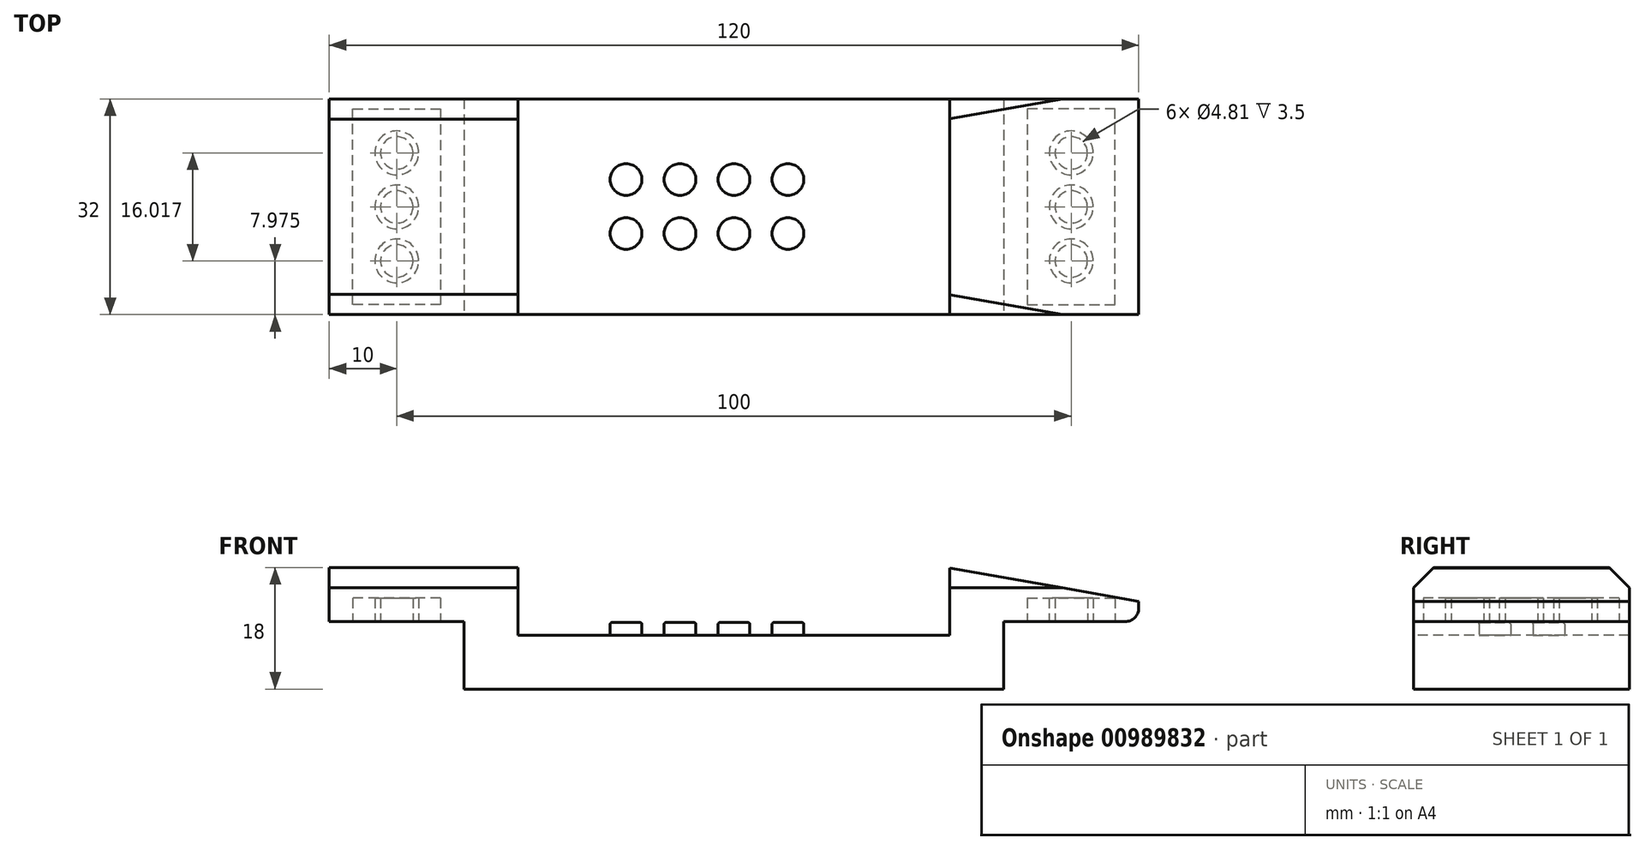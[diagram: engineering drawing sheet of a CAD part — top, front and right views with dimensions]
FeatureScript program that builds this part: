
annotation { "Feature Type Name" : "Feature", "Feature Type Description" : "" }
export const myFeature = defineFeature(function(context is Context, id is Id, definition is map)
    precondition{}
    {
        {
            var Q0;
            Q0=qCreatedBy(makeId("Front.planeOp"),FACE);
            var sketch = newSketch(context, id + "F0", { "sketchPlane" : qUnion([Q0])});
            skLineSegment(sketch, "E0", {"start": v(0, 0) * mm, "end": v(-40, 0) * mm});
            skLineSegment(sketch, "E1", {"start": v(-40, 0) * mm, "end": v(-40, 10) * mm});
            skLineSegment(sketch, "E2", {"start": v(-40, 10) * mm, "end": v(-60, 10) * mm});
            skLineSegment(sketch, "E3.0", {"start": v(-32, 18) * mm, "end": v(-60, 18) * mm});
            skLineSegment(sketch, "E3.1", {"start": v(-32, 8) * mm, "end": v(-32, 18) * mm});
            skLineSegment(sketch, "E3.2", {"start": v(0, 8) * mm, "end": v(-32, 8) * mm});
            skLineSegment(sketch, "E4", {"start": v(-60, 18) * mm, "end": v(-60, 10) * mm});
            skLineSegment(sketch, "E5", {"start": v(0, 8) * mm, "end": v(0, 0) * mm});
            skCircle(sketch, "E6", {"center": v(-50, 6) * mm, "radius": 10 * mm, "construction": true});
            skPoint(sketch, "E6.centerSnap0", {"position": v(-50, 10) * mm});
            skCircle(sketch, "E7", {"center": v(-50, 6) * mm, "radius": 12 * mm, "construction": true});
            skSolve(sketch);
        }
        {
            var Q0;
            Q0=makeQuery(id+"F0.imprint","IMPRINT",FACE,{"disambiguationData":[TD([[makeQuery(id+"F0.imprint","IMPRINT",EDGE,{"derivedFrom":sQuery(id+"F0.wireOp",EDGE,"E0")}),-1.0]])]});
            extrude(context, id + "F1", {"entities" : qUnion([Q0]), "oppositeDirection" : true, "depth" : 32 * mm, "offsetDistance" : 25 * mm});
        }
        {
            var Q0;
            Q0=makeQuery(id+"F1.opExtrude","SWEPT_FACE",FACE,{"disambiguationData":[OSD([sQuery(id+"F0.wireOp",EDGE,"E2")])]});
            var sketch = newSketch(context, id + "F2", { "sketchPlane" : qUnion([Q0])});
            skLineSegment(sketch, "E8", {"start": v(-43.5, -1.47) * mm, "end": v(-56.5, -1.47) * mm});
            skLineSegment(sketch, "E9", {"start": v(-56.5, -1.47) * mm, "end": v(-56.5, -30.5) * mm});
            skLineSegment(sketch, "E10", {"start": v(-56.5, -30.5) * mm, "end": v(-43.5, -30.5) * mm});
            skLineSegment(sketch, "E11", {"start": v(-43.5, -30.5) * mm, "end": v(-43.5, -1.47) * mm});
            skCircle(sketch, "E12.0", {"center": v(-50, -7.97) * mm, "radius": 2.4 * mm});
            skCircle(sketch, "E13.0", {"center": v(-50, -7.97) * mm, "radius": 3.25 * mm});
            skCircle(sketch, "E14.0", {"center": v(-50, -15.98) * mm, "radius": 2.4 * mm});
            skCircle(sketch, "E15.0", {"center": v(-50, -15.98) * mm, "radius": 3.25 * mm});
            skCircle(sketch, "E16.0", {"center": v(-50, -24) * mm, "radius": 2.4 * mm});
            skCircle(sketch, "E17.0", {"center": v(-50, -24) * mm, "radius": 3.25 * mm});
            skLineSegment(sketch, "E18.0", {"start": v(-42, 0.03) * mm, "end": v(-42, -32) * mm, "construction": true});
            skLineSegment(sketch, "E18.1", {"start": v(-42, 0.03) * mm, "end": v(-58, 0.03) * mm, "construction": true});
            skLineSegment(sketch, "E18.2", {"start": v(-58, 0.03) * mm, "end": v(-58, -32) * mm, "construction": true});
            skLineSegment(sketch, "E18.3", {"start": v(-42, -32) * mm, "end": v(-58, -32) * mm, "construction": true});
            skSolve(sketch);
        }
        {
            var Q0;
            Q0=makeQuery(id+"F2.imprint","IMPRINT",FACE,{"disambiguationData":[TD([[makeQuery(id+"F2.imprint","IMPRINT",EDGE,{"derivedFrom":sQuery(id+"F2.wireOp",EDGE,"E8")}),1.0]])]});
            var Q1;
            Q1=makeQuery(id+"F2.imprint","IMPRINT",FACE,{"disambiguationData":[TD([[makeQuery(id+"F2.imprint","IMPRINT",EDGE,{"derivedFrom":sQuery(id+"F2.wireOp",EDGE,"E14.0")}),1.0]])]});
            var Q2;
            Q2=makeQuery(id+"F2.imprint","IMPRINT",FACE,{"disambiguationData":[TD([[makeQuery(id+"F2.imprint","IMPRINT",EDGE,{"derivedFrom":sQuery(id+"F2.wireOp",EDGE,"E12.0")}),1.0]])]});
            var Q3;
            Q3=makeQuery(id+"F2.imprint","IMPRINT",FACE,{"disambiguationData":[TD([[makeQuery(id+"F2.imprint","IMPRINT",EDGE,{"derivedFrom":sQuery(id+"F2.wireOp",EDGE,"E16.0")}),1.0]])]});
            extrude(context, id + "F3", {"entities" : qUnion([Q0, Q1, Q2, Q3]), "operationType" : NewBodyOperationType.REMOVE, "oppositeDirection" : true, "depth" : 3.5 * mm, "offsetDistance" : 25 * mm});
        }
        {
            var Q0;
            Q0=makeQuery(id+"F1.opExtrude","SWEPT_BODY",BODY,{"disambiguationData":[OSD([sQuery(id+"F0.wireOp",EDGE,"E0"),sQuery(id+"F0.wireOp",EDGE,"E1"),sQuery(id+"F0.wireOp",EDGE,"E2"),sQuery(id+"F0.wireOp",EDGE,"E3.0"),sQuery(id+"F0.wireOp",EDGE,"E3.1"),sQuery(id+"F0.wireOp",EDGE,"E3.2"),sQuery(id+"F0.wireOp",EDGE,"E4"),sQuery(id+"F0.wireOp",EDGE,"E5")])]});
            var Q1;
            Q1=makeQuery(id+"F1.opExtrude","SWEPT_FACE",FACE,{"disambiguationData":[OSD([sQuery(id+"F0.wireOp",EDGE,"E5")])]});
            mirror(context, id + "F4", {"operationType" : NewBodyOperationType.ADD, "entities" : qUnion([Q0]), "mirrorPlane" : qUnion([Q1])});
        }
        {
            var Q0;
            {var subQ0=makeQuery(id+"F1.opExtrude","SWEPT_FACE",FACE,{"disambiguationData":[OSD([sQuery(id+"F0.wireOp",EDGE,"E3.2")])]});Q0=makeQuery(id+"F4.boolean.opBoolean","MERGE",FACE,{"derivedFrom":[subQ0,makeQuery(id+"F4.opPattern","COPY",FACE,{"derivedFrom":subQ0,"instanceName":"1"})]});}
            var sketch = newSketch(context, id + "F5", { "sketchPlane" : qUnion([Q0])});
            skLineSegment(sketch, "E19.0", {"start": v(-19.9, 7.93) * mm, "end": v(12.1, 7.93) * mm, "construction": true});
            skLineSegment(sketch, "E19.1", {"start": v(-19.9, 7.93) * mm, "end": v(-19.9, 23.93) * mm, "construction": true});
            skLineSegment(sketch, "E19.2", {"start": v(-19.9, 23.93) * mm, "end": v(12.1, 23.93) * mm, "construction": true});
            skLineSegment(sketch, "E19.3", {"start": v(12.1, 7.93) * mm, "end": v(12.1, 23.93) * mm, "construction": true});
            skCircle(sketch, "E19.4", {"center": v(8, 12.03) * mm, "radius": 2.35 * mm});
            skCircle(sketch, "E19.5", {"center": v(8, 20.03) * mm, "radius": 2.35 * mm});
            skCircle(sketch, "E19.6", {"center": v(0, 20.03) * mm, "radius": 2.35 * mm});
            skCircle(sketch, "E19.7", {"center": v(0, 12.03) * mm, "radius": 2.35 * mm});
            skCircle(sketch, "E19.8", {"center": v(-8, 12.03) * mm, "radius": 2.35 * mm});
            skCircle(sketch, "E19.9", {"center": v(-8, 20.03) * mm, "radius": 2.35 * mm});
            skCircle(sketch, "E19.10", {"center": v(-16, 20.03) * mm, "radius": 2.35 * mm});
            skCircle(sketch, "E19.11", {"center": v(-16, 12.03) * mm, "radius": 2.35 * mm});
            skSolve(sketch);
        }
        {
            var Q0;
            Q0=makeQuery(id+"F5.imprint","IMPRINT",FACE,{"disambiguationData":[TD([[makeQuery(id+"F5.imprint","IMPRINT",EDGE,{"derivedFrom":sQuery(id+"F5.wireOp",EDGE,"E19.11")}),1.0]])]});
            var Q1;
            Q1=makeQuery(id+"F5.imprint","IMPRINT",FACE,{"disambiguationData":[TD([[makeQuery(id+"F5.imprint","IMPRINT",EDGE,{"derivedFrom":sQuery(id+"F5.wireOp",EDGE,"E19.10")}),1.0]])]});
            var Q2;
            Q2=makeQuery(id+"F5.imprint","IMPRINT",FACE,{"disambiguationData":[TD([[makeQuery(id+"F5.imprint","IMPRINT",EDGE,{"derivedFrom":sQuery(id+"F5.wireOp",EDGE,"E19.9")}),1.0]])]});
            var Q3;
            Q3=makeQuery(id+"F5.imprint","IMPRINT",FACE,{"disambiguationData":[TD([[makeQuery(id+"F5.imprint","IMPRINT",EDGE,{"derivedFrom":sQuery(id+"F5.wireOp",EDGE,"E19.8")}),1.0]])]});
            var Q4;
            Q4=makeQuery(id+"F5.imprint","IMPRINT",FACE,{"disambiguationData":[TD([[makeQuery(id+"F5.imprint","IMPRINT",EDGE,{"derivedFrom":sQuery(id+"F5.wireOp",EDGE,"E19.7")}),1.0]])]});
            var Q5;
            Q5=makeQuery(id+"F5.imprint","IMPRINT",FACE,{"disambiguationData":[TD([[makeQuery(id+"F5.imprint","IMPRINT",EDGE,{"derivedFrom":sQuery(id+"F5.wireOp",EDGE,"E19.6")}),1.0]])]});
            var Q6;
            Q6=makeQuery(id+"F5.imprint","IMPRINT",FACE,{"disambiguationData":[TD([[makeQuery(id+"F5.imprint","IMPRINT",EDGE,{"derivedFrom":sQuery(id+"F5.wireOp",EDGE,"E19.5")}),1.0]])]});
            var Q7;
            Q7=makeQuery(id+"F5.imprint","IMPRINT",FACE,{"disambiguationData":[TD([[makeQuery(id+"F5.imprint","IMPRINT",EDGE,{"derivedFrom":sQuery(id+"F5.wireOp",EDGE,"E19.4")}),1.0]])]});
            extrude(context, id + "F6", {"entities" : qUnion([Q0, Q1, Q2, Q3, Q4, Q5, Q6, Q7]), "operationType" : NewBodyOperationType.ADD, "depth" : 1.85 * mm, "offsetDistance" : 25 * mm});
        }
        {
            var Q0;
            Q0=makeQuery(id+"F1.opExtrude","CAP_EDGE",EDGE,{"disambiguationData":[OSD([sQuery(id+"F0.wireOp",EDGE,"E3.0")])],"isStart":true});
            var Q1;
            Q1=makeQuery(id+"F1.opExtrude","CAP_EDGE",EDGE,{"disambiguationData":[OSD([sQuery(id+"F0.wireOp",EDGE,"E3.0")])],"isStart":false});
            var Q2;
            Q2=makeQuery(id+"F4.opPattern","COPY",EDGE,{"derivedFrom":makeQuery(id+"F1.opExtrude","CAP_EDGE",EDGE,{"disambiguationData":[OSD([sQuery(id+"F0.wireOp",EDGE,"E3.0")])],"isStart":true}),"instanceName":"1"});
            var Q3;
            Q3=makeQuery(id+"F4.opPattern","COPY",EDGE,{"derivedFrom":makeQuery(id+"F1.opExtrude","CAP_EDGE",EDGE,{"disambiguationData":[OSD([sQuery(id+"F0.wireOp",EDGE,"E3.0")])],"isStart":false}),"instanceName":"1"});
            chamfer(context, id + "F7", {"entities" : qUnion([Q0, Q1, Q2, Q3]), "width" : 3 * mm, "tangentPropagation" : true});
        }
        {
            var Q0;
            {var subQ0=sQuery(id+"F0.wireOp",EDGE,"E4");Q0=makeQuery(id+"F7.opChamfer","BLEND_EDGE",EDGE,{"blendedFrom":[makeQuery(id+"F4.opPattern","COPY",EDGE,{"derivedFrom":makeQuery(id+"F1.opExtrude","SWEPT_EDGE",EDGE,{"disambiguationData":[OSD([sQuery(id+"F0.wireOp",EDGE,"E3.0"),subQ0])]}),"instanceName":"1"}),makeQuery(id+"F4.opPattern","COPY",FACE,{"derivedFrom":makeQuery(id+"F1.opExtrude","SWEPT_FACE",FACE,{"disambiguationData":[OSD([subQ0])]}),"instanceName":"1"})],"blendedInto":[makeQuery(id+"F4.opPattern","COPY",FACE,{"derivedFrom":makeQuery(id+"F1.opExtrude","SWEPT_FACE",FACE,{"disambiguationData":[OSD([subQ0])]}),"instanceName":"1"})]});}
            var Q1;
            Q1=makeQuery(id+"F4.opPattern","COPY",EDGE,{"derivedFrom":makeQuery(id+"F1.opExtrude","SWEPT_EDGE",EDGE,{"disambiguationData":[OSD([sQuery(id+"F0.wireOp",EDGE,"E2"),sQuery(id+"F0.wireOp",EDGE,"E4")])]}),"instanceName":"1"});
            var Q2;
            {var subQ0=sQuery(id+"F0.wireOp",EDGE,"E3.0");Q2=makeQuery(id+"F7.opChamfer","BLEND_EDGE",EDGE,{"blendedFrom":[makeQuery(id+"F4.opPattern","COPY",EDGE,{"derivedFrom":makeQuery(id+"F1.opExtrude","SWEPT_EDGE",EDGE,{"disambiguationData":[OSD([subQ0,sQuery(id+"F0.wireOp",EDGE,"E4")])]}),"instanceName":"1"}),makeQuery(id+"F4.opPattern","COPY",FACE,{"derivedFrom":makeQuery(id+"F1.opExtrude","SWEPT_FACE",FACE,{"disambiguationData":[OSD([subQ0])]}),"instanceName":"1"})],"blendedInto":[makeQuery(id+"F4.opPattern","COPY",FACE,{"derivedFrom":makeQuery(id+"F1.opExtrude","SWEPT_FACE",FACE,{"disambiguationData":[OSD([subQ0])]}),"instanceName":"1"})]});}
            fillet(context, id + "F8", {"entities" : qUnion([Q0, Q1, Q2]), "radius" : 2 * mm, "tangentPropagation" : true, "allowEdgeOverflow" : false});
        }
        {
            var Q0;
            Q0=makeQuery(id+"F4.opPattern","COPY",EDGE,{"derivedFrom":makeQuery(id+"F1.opExtrude","SWEPT_EDGE",EDGE,{"disambiguationData":[OSD([sQuery(id+"F0.wireOp",EDGE,"E3.0"),sQuery(id+"F0.wireOp",EDGE,"E4")])]}),"instanceName":"1"});
            chamfer(context, id + "F9", {"entities" : qUnion([Q0]), "chamferType" : ChamferType.OFFSET_ANGLE, "width" : 5 * mm, "oppositeDirection" : false, "angle" : 80 * degree, "tangentPropagation" : true});
        }
        {
            var Q0;
            Q0=makeQuery(id+"F6.opExtrude","CAP_EDGE",EDGE,{"disambiguationData":[OSD([sQuery(id+"F5.wireOp",EDGE,"E19.11")])],"isStart":false});
            var Q1;
            Q1=makeQuery(id+"F6.opExtrude","CAP_EDGE",EDGE,{"disambiguationData":[OSD([sQuery(id+"F5.wireOp",EDGE,"E19.10")])],"isStart":false});
            var Q2;
            Q2=makeQuery(id+"F6.opExtrude","CAP_EDGE",EDGE,{"disambiguationData":[OSD([sQuery(id+"F5.wireOp",EDGE,"E19.9")])],"isStart":false});
            var Q3;
            Q3=makeQuery(id+"F6.opExtrude","CAP_EDGE",EDGE,{"disambiguationData":[OSD([sQuery(id+"F5.wireOp",EDGE,"E19.8")])],"isStart":false});
            var Q4;
            Q4=makeQuery(id+"F6.opExtrude","CAP_EDGE",EDGE,{"disambiguationData":[OSD([sQuery(id+"F5.wireOp",EDGE,"E19.7")])],"isStart":false});
            var Q5;
            Q5=makeQuery(id+"F6.opExtrude","CAP_EDGE",EDGE,{"disambiguationData":[OSD([sQuery(id+"F5.wireOp",EDGE,"E19.4")])],"isStart":false});
            var Q6;
            Q6=makeQuery(id+"F6.opExtrude","CAP_EDGE",EDGE,{"disambiguationData":[OSD([sQuery(id+"F5.wireOp",EDGE,"E19.5")])],"isStart":false});
            var Q7;
            Q7=makeQuery(id+"F6.opExtrude","CAP_EDGE",EDGE,{"disambiguationData":[OSD([sQuery(id+"F5.wireOp",EDGE,"E19.6")])],"isStart":false});
            fillet(context, id + "F10", {"entities" : qUnion([Q0, Q1, Q2, Q3, Q4, Q5, Q6, Q7]), "radius" : .25 * mm, "tangentPropagation" : true, "allowEdgeOverflow" : false});
        }
    });
